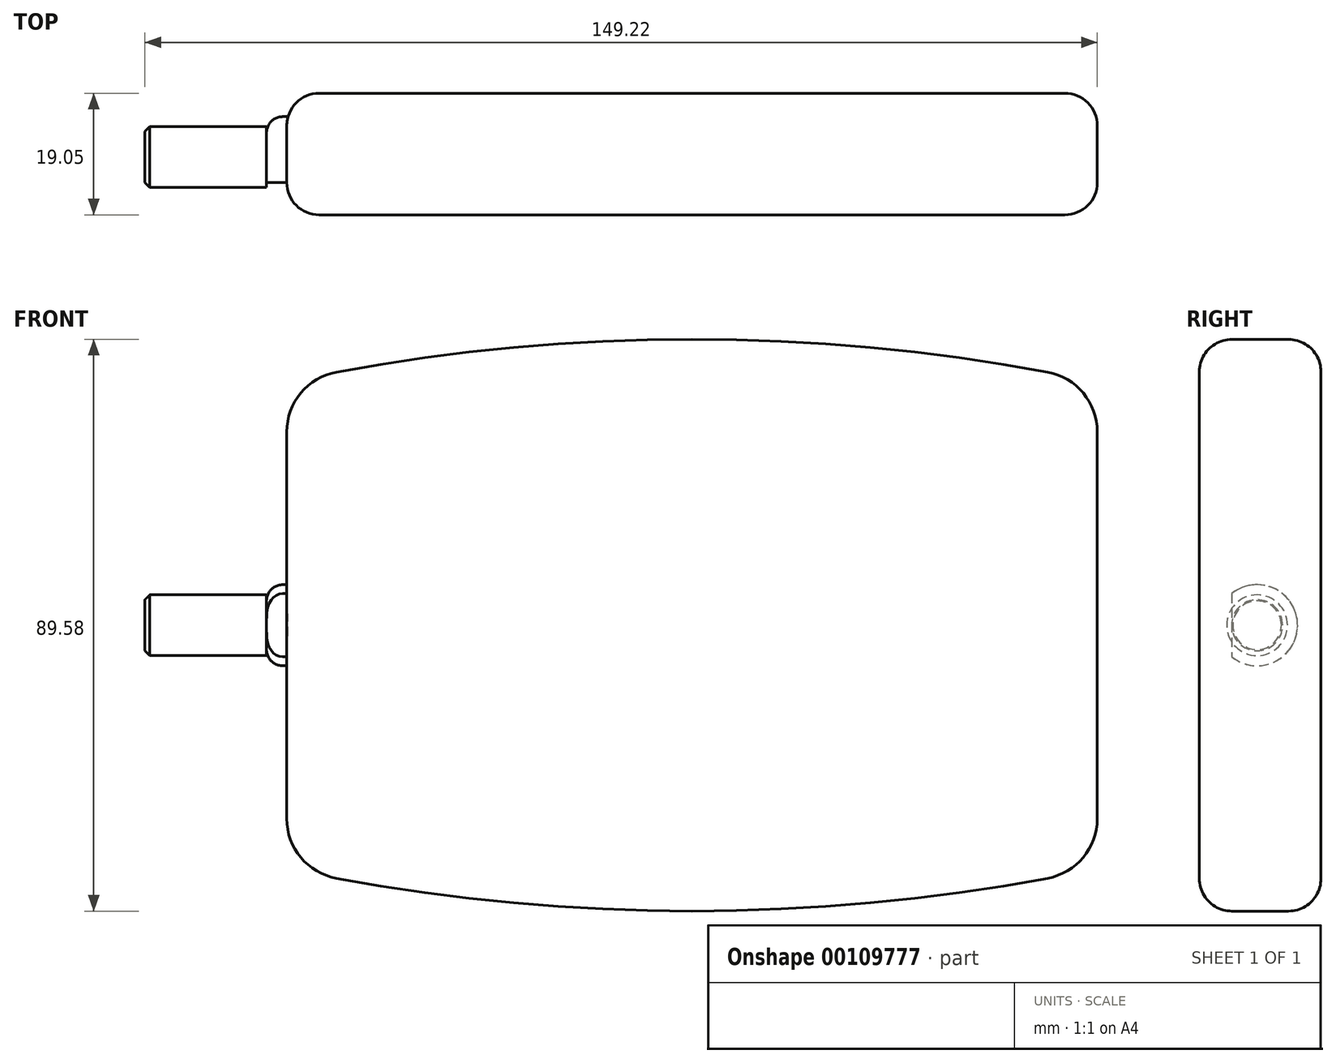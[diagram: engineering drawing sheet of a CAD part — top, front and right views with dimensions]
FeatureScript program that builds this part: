
annotation { "Feature Type Name" : "Feature", "Feature Type Description" : "" }
export const myFeature = defineFeature(function(context is Context, id is Id, definition is map)
    precondition{}
    {
        {
            var Q0;
            Q0=qCreatedBy(makeId("Front.planeOp"),FACE);
            var sketch = newSketch(context, id + "F0", { "sketchPlane" : qUnion([Q0])});
            skArc(sketch, "E0", {"start": v(71.91, 38.1) * mm, "mid": v(8.41, 44.79) * mm, "end": v(-55.09, 38.1) * mm});
            skLineSegment(sketch, "E1", {"start": v(-55.09, 38.1) * mm, "end": v(-55.09, 0) * mm});
            skLineSegment(sketch, "E2", {"start": v(71.91, 38.1) * mm, "end": v(71.91, 0) * mm});
            skLineSegment(sketch, "E3.MirrorCS", {"start": v(-55.09, -38.1) * mm, "end": v(-55.09, 0) * mm});
            skArc(sketch, "E4.MirrorCS", {"start": v(71.91, -38.1) * mm, "mid": v(8.41, -44.79) * mm, "end": v(-55.09, -38.1) * mm});
            skLineSegment(sketch, "E5.MirrorCS", {"start": v(71.91, -38.1) * mm, "end": v(71.91, 0) * mm});
            skSolve(sketch);
        }
        {
            var Q0;
            Q0 = qSketchRegion(id + "F0", true);
            extrude(context, id + "F1", {"entities" : qUnion([Q0]), "depth" : 19.05 * mm});
        }
        {
            var Q0;
            Q0=makeQuery(id+"F1.opExtrude","SWEPT_EDGE",EDGE,{"disambiguationData":[OSD([sQuery(id+"F0.wireOp",EDGE,"E0"),sQuery(id+"F0.wireOp",EDGE,"E1")])]});
            var Q1;
            Q1=makeQuery(id+"F1.opExtrude","SWEPT_EDGE",EDGE,{"disambiguationData":[OSD([sQuery(id+"F0.wireOp",EDGE,"E3.MirrorCS"),sQuery(id+"F0.wireOp",EDGE,"E4.MirrorCS")])]});
            var Q2;
            Q2=makeQuery(id+"F1.opExtrude","SWEPT_EDGE",EDGE,{"disambiguationData":[OSD([sQuery(id+"F0.wireOp",EDGE,"E0"),sQuery(id+"F0.wireOp",EDGE,"E2")])]});
            var Q3;
            Q3=makeQuery(id+"F1.opExtrude","SWEPT_EDGE",EDGE,{"disambiguationData":[OSD([sQuery(id+"F0.wireOp",EDGE,"E4.MirrorCS"),sQuery(id+"F0.wireOp",EDGE,"E5.MirrorCS")])]});
            fillet(context, id + "F2", {"entities" : qUnion([Q0, Q1, Q2, Q3]), "radius" : 9.52 * mm, "tangentPropagation" : true, "allowEdgeOverflow" : false});
        }
        {
            var Q0;
            Q0=makeQuery(id+"F1.opExtrude","CAP_EDGE",EDGE,{"disambiguationData":[OSD([sQuery(id+"F0.wireOp",EDGE,"E0")])],"isStart":false});
            var Q1;
            Q1=makeQuery(id+"F1.opExtrude","CAP_EDGE",EDGE,{"disambiguationData":[OSD([sQuery(id+"F0.wireOp",EDGE,"E0")])],"isStart":true});
            fillet(context, id + "F3", {"entities" : qUnion([Q0, Q1]), "radius" : 5.08 * mm, "tangentPropagation" : true, "allowEdgeOverflow" : false});
        }
        {
            var Q0;
            Q0=makeQuery(id+"F1.opExtrude","SWEPT_FACE",FACE,{"disambiguationData":[OSD([sQuery(id+"F0.wireOp",EDGE,"E1"),sQuery(id+"F0.wireOp",EDGE,"E3.MirrorCS")])]});
            var sketch = newSketch(context, id + "F4", { "sketchPlane" : qUnion([Q0])});
            skCircle(sketch, "E6", {"center": v(10, 0) * mm, "radius": 6.35 * mm});
            skSolve(sketch);
        }
        {
            var Q0;
            {var subQ0=sQuery(id+"F4.wireOp",EDGE,"E6");var subQ1=sQuery(id+"F0.wireOp",EDGE,"E3.MirrorCS");var subQ2=sQuery(id+"F0.wireOp",EDGE,"E1");var subQ3=makeQuery(id+"F3.opFillet","BLEND_EDGE",EDGE,{"blendedFrom":[makeQuery(id+"F1.opExtrude","CAP_EDGE",EDGE,{"disambiguationData":[OSD([subQ2,subQ1])],"isStart":false}),makeQuery(id+"F1.opExtrude","SWEPT_FACE",FACE,{"disambiguationData":[OSD([subQ2,subQ1])]})],"blendedInto":[makeQuery(id+"F1.opExtrude","SWEPT_FACE",FACE,{"disambiguationData":[OSD([subQ2,subQ1])]})]});var subQ4=makeQuery(id+"F4.imprint","INTERSECT",VERTEX,{"disambiguationData":[OD(0.0)],"derivedFrom":[subQ3,subQ0]});Q0=makeQuery(id+"F4.imprint","IMPRINT",FACE,{"disambiguationData":[TD([[makeQuery(id+"F4.imprint","IMPRINT",EDGE,{"disambiguationData":[TD([[subQ4,1.0]])],"derivedFrom":subQ0}),1.0]])]});}
            var Q1;
            {var subQ0=sQuery(id+"F4.wireOp",EDGE,"E6");var subQ1=sQuery(id+"F0.wireOp",EDGE,"E3.MirrorCS");var subQ2=sQuery(id+"F0.wireOp",EDGE,"E1");var subQ3=makeQuery(id+"F1.opExtrude","SWEPT_FACE",FACE,{"disambiguationData":[OSD([subQ2,subQ1])]});var subQ4=makeQuery(id+"F3.opFillet","BLEND_EDGE",EDGE,{"blendedFrom":[makeQuery(id+"F1.opExtrude","CAP_EDGE",EDGE,{"disambiguationData":[OSD([subQ2,subQ1])],"isStart":true}),subQ3],"blendedInto":[subQ3]});var subQ5=makeQuery(id+"F4.imprint","INTERSECT",VERTEX,{"disambiguationData":[OD(0.0)],"derivedFrom":[subQ4,subQ0]});Q1=makeQuery(id+"F4.imprint","IMPRINT",FACE,{"disambiguationData":[TD([[makeQuery(id+"F4.imprint","IMPRINT",EDGE,{"disambiguationData":[TD([[subQ5,1.0]])],"derivedFrom":subQ0}),1.0]])]});}
            var Q2;
            {var subQ0=sQuery(id+"F4.wireOp",EDGE,"E6");var subQ1=sQuery(id+"F0.wireOp",EDGE,"E3.MirrorCS");var subQ2=sQuery(id+"F0.wireOp",EDGE,"E1");var subQ3=makeQuery(id+"F3.opFillet","BLEND_EDGE",EDGE,{"blendedFrom":[makeQuery(id+"F1.opExtrude","CAP_EDGE",EDGE,{"disambiguationData":[OSD([subQ2,subQ1])],"isStart":true}),makeQuery(id+"F1.opExtrude","SWEPT_FACE",FACE,{"disambiguationData":[OSD([subQ2,subQ1])]})],"blendedInto":[makeQuery(id+"F1.opExtrude","SWEPT_FACE",FACE,{"disambiguationData":[OSD([subQ2,subQ1])]})]});var subQ4=makeQuery(id+"F4.imprint","INTERSECT",VERTEX,{"disambiguationData":[OD(0.0)],"derivedFrom":[subQ3,subQ0]});Q2=makeQuery(id+"F4.imprint","IMPRINT",FACE,{"disambiguationData":[TD([[makeQuery(id+"F4.imprint","IMPRINT",EDGE,{"disambiguationData":[TD([[subQ4,-1.0]])],"derivedFrom":subQ0}),1.0]])]});}
            extrude(context, id + "F5", {"entities" : qUnion([Q0, Q1, Q2]), "operationType" : NewBodyOperationType.ADD, "depth" : 3.17 * mm, "hasSecondDirection" : true, "secondDirectionOppositeDirection" : true, "secondDirectionDepth" : 5.08 * mm});
        }
        {
            var Q0;
            Q0=makeQuery(id+"F5.opExtrude","CAP_EDGE",EDGE,{"disambiguationData":[OSD([sQuery(id+"F4.wireOp",EDGE,"E6")])],"isStart":false});
            fillet(context, id + "F6", {"entities" : qUnion([Q0]), "radius" : 2.54 * mm, "tangentPropagation" : true, "allowEdgeOverflow" : false});
        }
        {
            var Q0;
            Q0=makeQuery(id+"F5.opExtrude","CAP_FACE",FACE,{"disambiguationData":[OSD([sQuery(id+"F4.wireOp",EDGE,"E6")])],"isStart":false});
            var sketch = newSketch(context, id + "F7", { "sketchPlane" : qUnion([Q0])});
            skCircle(sketch, "E7", {"center": v(10, 0) * mm, "radius": 4.76 * mm});
            skSolve(sketch);
        }
        {
            var Q0;
            Q0 = qSketchRegion(id + "F7", true);
            extrude(context, id + "F8", {"entities" : qUnion([Q0]), "operationType" : NewBodyOperationType.ADD, "depth" : 19.05 * mm});
        }
        {
            var Q0;
            Q0=makeQuery(id+"F8.opExtrude","CAP_EDGE",EDGE,{"disambiguationData":[OSD([sQuery(id+"F7.wireOp",EDGE,"E7")])],"isStart":false});
            chamfer(context, id + "F9", {"entities" : qUnion([Q0]), "width" : 0.76 * mm, "tangentPropagation" : true});
        }
    });
